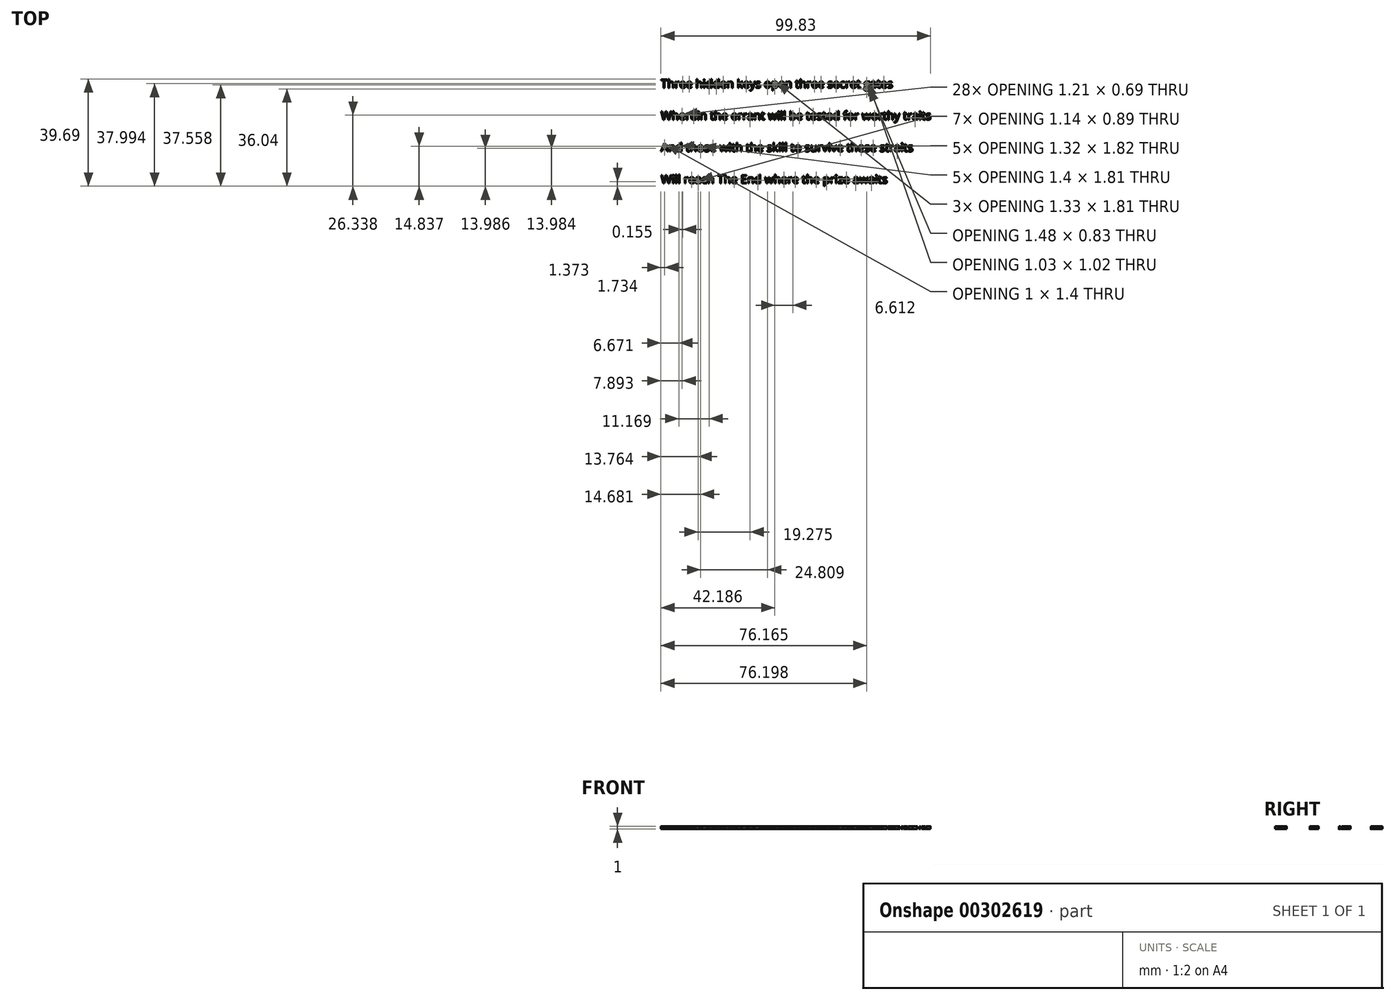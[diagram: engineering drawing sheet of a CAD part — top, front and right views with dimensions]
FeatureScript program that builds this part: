
annotation { "Feature Type Name" : "Feature", "Feature Type Description" : "" }
export const myFeature = defineFeature(function(context is Context, id is Id, definition is map)
    precondition{}
    {
        {
            var Q0;
            Q0=qCreatedBy(makeId("Top.planeOp"),FACE);
            var sketch = newSketch(context, id + "F0", { "sketchPlane" : qUnion([Q0])});
            skText(sketch, "E0", { "text": "Three hidden keys open three secret gates\n\nWherein the errant will be tested for worthy traits\n\nAnd those with the skill to survive these straits\n\nWill reach The End where the prize awaits ", "fontName": "OpenSans-Regular.ttf"});
            const initialGuessF0  = {"E0": [-0.05032, 0.01133, 1, 0, 0.00312]};
            skSetInitialGuess(sketch, initialGuessF0);
            skSolve(sketch);
        }
        {
            var Q0;
            Q0 = qSketchRegion(id + "F0", true);
            extrude(context, id + "F1", {"entities" : qUnion([Q0]), "depth" : 1 * mm});
        }
    });
